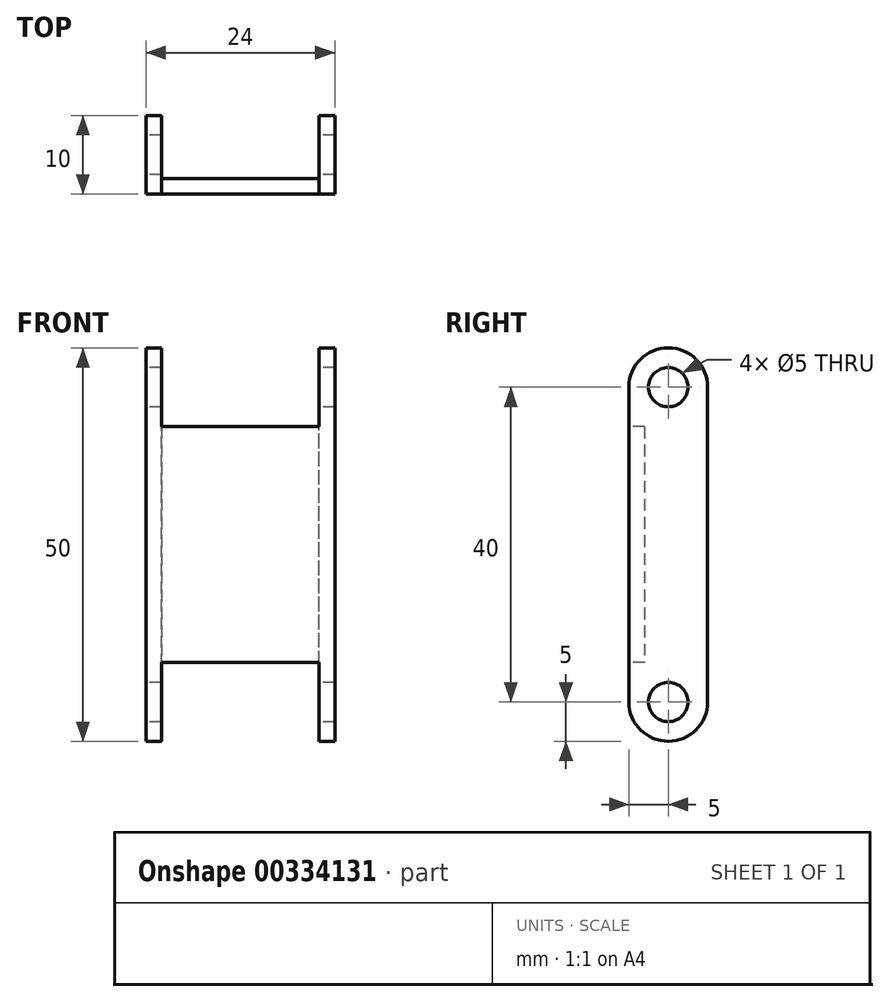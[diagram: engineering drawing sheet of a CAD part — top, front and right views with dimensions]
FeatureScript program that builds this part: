
annotation { "Feature Type Name" : "Feature", "Feature Type Description" : "" }
export const myFeature = defineFeature(function(context is Context, id is Id, definition is map)
    precondition{}
    {
        {
            var Q0;
            Q0=qCreatedBy(makeId("Front.planeOp"),FACE);
            var sketch = newSketch(context, id + "F0", { "sketchPlane" : qUnion([Q0])});
            skLineSegment(sketch, "E0.bottom", {"start": v(0, 0) * mm, "end": v(2, 0) * mm});
            skLineSegment(sketch, "E0.top", {"start": v(0, 50) * mm, "end": v(2, 50) * mm});
            skLineSegment(sketch, "E0.left", {"start": v(0, 0) * mm, "end": v(0, 50) * mm});
            skLineSegment(sketch, "E0.right", {"start": v(2, 0) * mm, "end": v(2, 50) * mm});
            skLineSegment(sketch, "E1.bottom", {"start": v(2, 40) * mm, "end": v(22, 40) * mm});
            skLineSegment(sketch, "E1.top", {"start": v(2, 10) * mm, "end": v(22, 10) * mm});
            skLineSegment(sketch, "E1.left", {"start": v(2, 40) * mm, "end": v(2, 10) * mm});
            skLineSegment(sketch, "E1.right", {"start": v(22, 40) * mm, "end": v(22, 10) * mm});
            skPoint(sketch, "E1.middle", {"position": v(12, 25) * mm});
            skPoint(sketch, "E1.middle.positionSnap0", {"position": v(2, 25) * mm});
            skPoint(sketch, "E1.centerSnap0", {"position": v(2, 25) * mm});
            skLineSegment(sketch, "E2", {"start": v(12, 42.57) * mm, "end": v(12, 7.33) * mm, "construction": true});
            skLineSegment(sketch, "E3.MirrorCS", {"start": v(22, 0) * mm, "end": v(22, 50) * mm});
            skLineSegment(sketch, "E4.MirrorCS", {"start": v(24, 50) * mm, "end": v(22, 50) * mm});
            skLineSegment(sketch, "E5.MirrorCS", {"start": v(24, 0) * mm, "end": v(24, 50) * mm});
            skLineSegment(sketch, "E6.MirrorCS", {"start": v(24, 0) * mm, "end": v(22, 0) * mm});
            skSolve(sketch);
        }
        {
            var Q0;
            {var subQ1=sQuery(id+"F0.wireOp",EDGE,"E0.bottom");Q0=makeQuery(id+"F0.imprint","IMPRINT",FACE,{"disambiguationData":[TD([[makeQuery(id+"F0.imprint","IMPRINT",EDGE,{"derivedFrom":subQ1}),1.0]])]});}
            var Q1;
            {var subQ0=sQuery(id+"F0.wireOp",EDGE,"E4.MirrorCS");Q1=makeQuery(id+"F0.imprint","IMPRINT",FACE,{"disambiguationData":[TD([[makeQuery(id+"F0.imprint","IMPRINT",EDGE,{"derivedFrom":subQ0}),1.0]])]});}
            extrude(context, id + "F1", {"entities" : qUnion([Q0, Q1]), "depth" : 10 * mm, "symmetric" : true});
        }
        {
            var Q0;
            Q0=makeQuery(id+"F1.opExtrude","SWEPT_FACE",FACE,{"disambiguationData":[OSD([sQuery(id+"F0.wireOp",EDGE,"E0.left")])]});
            var sketch = newSketch(context, id + "F2", { "sketchPlane" : qUnion([Q0])});
            skArc(sketch, "E7", {"start": v(-5, 5) * mm, "mid": v(0, 0) * mm, "end": v(5, 5) * mm});
            skLineSegment(sketch, "E8.0", {"start": v(5, 0) * mm, "end": v(5, 5) * mm});
            skLineSegment(sketch, "E9.0", {"start": v(-5, 0) * mm, "end": v(-5, 5) * mm});
            skLineSegment(sketch, "E10.0", {"start": v(5, 0) * mm, "end": v(-5, 0) * mm});
            skPoint(sketch, "E11.orphan", {"position": v(5, 50) * mm});
            skPoint(sketch, "E12.orphan", {"position": v(-5, 50) * mm});
            skSolve(sketch);
        }
        {
            var Q0;
            Q0 = qSketchRegion(id + "F2", true);
            extrude(context, id + "F3", {"entities" : qUnion([Q0]), "operationType" : NewBodyOperationType.REMOVE, "oppositeDirection" : true, "depth" : 25 * mm});
        }
        {
            var Q0;
            Q0=makeQuery(id+"F1.opExtrude","SWEPT_FACE",FACE,{"disambiguationData":[OSD([sQuery(id+"F0.wireOp",EDGE,"E0.left")])]});
            var sketch = newSketch(context, id + "F4", { "sketchPlane" : qUnion([Q0])});
            skArc(sketch, "E13", {"start": v(5, 45) * mm, "mid": v(0, 50) * mm, "end": v(-5, 45) * mm});
            skLineSegment(sketch, "E14.0", {"start": v(5, 50) * mm, "end": v(-5, 50) * mm});
            skLineSegment(sketch, "E15.0", {"start": v(-5, 45) * mm, "end": v(-5, 50) * mm});
            skLineSegment(sketch, "E16.0", {"start": v(5, 45) * mm, "end": v(5, 50) * mm});
            skPoint(sketch, "E17.orphan", {"position": v(5, 5) * mm});
            skPoint(sketch, "E18.orphan", {"position": v(-5, 5) * mm});
            skSolve(sketch);
        }
        {
            var Q0;
            Q0 = qSketchRegion(id + "F4", true);
            extrude(context, id + "F5", {"entities" : qUnion([Q0]), "operationType" : NewBodyOperationType.REMOVE, "oppositeDirection" : true, "depth" : 25 * mm});
        }
        {
            var Q0;
            Q0=makeQuery(id+"F1.opExtrude","SWEPT_FACE",FACE,{"disambiguationData":[OSD([sQuery(id+"F0.wireOp",EDGE,"E0.left")])]});
            var sketch = newSketch(context, id + "F6", { "sketchPlane" : qUnion([Q0])});
            skCircle(sketch, "E19", {"center": v(0, 45) * mm, "radius": 2.5 * mm});
            skSolve(sketch);
        }
        {
            var Q0;
            Q0 = qSketchRegion(id + "F6", true);
            extrude(context, id + "F7", {"entities" : qUnion([Q0]), "operationType" : NewBodyOperationType.REMOVE, "oppositeDirection" : true, "depth" : 25 * mm});
        }
        {
            var Q0;
            Q0=makeQuery(id+"F1.opExtrude","SWEPT_FACE",FACE,{"disambiguationData":[OSD([sQuery(id+"F0.wireOp",EDGE,"E0.left")])]});
            var sketch = newSketch(context, id + "F8", { "sketchPlane" : qUnion([Q0])});
            skCircle(sketch, "E20", {"center": v(0, 5) * mm, "radius": 2.5 * mm});
            skSolve(sketch);
        }
        {
            var Q0;
            Q0 = qSketchRegion(id + "F8", true);
            extrude(context, id + "F9", {"entities" : qUnion([Q0]), "operationType" : NewBodyOperationType.REMOVE, "oppositeDirection" : true, "depth" : 25 * mm});
        }
        {
            var Q0;
            Q0=makeQuery(id+"F1.opExtrude","CAP_FACE",FACE,{"disambiguationData":[OSD([sQuery(id+"F0.wireOp",EDGE,"E3.MirrorCS"),sQuery(id+"F0.wireOp",EDGE,"E4.MirrorCS"),sQuery(id+"F0.wireOp",EDGE,"E5.MirrorCS"),sQuery(id+"F0.wireOp",EDGE,"E6.MirrorCS")])],"isStart":false});
            var sketch = newSketch(context, id + "F10", { "sketchPlane" : qUnion([Q0])});
            skLineSegment(sketch, "E21.0", {"start": v(2, 40) * mm, "end": v(22, 40) * mm});
            skLineSegment(sketch, "E22.0", {"start": v(2, 10) * mm, "end": v(22, 10) * mm});
            skLineSegment(sketch, "E23.0", {"start": v(2, 40) * mm, "end": v(2, 10) * mm});
            skLineSegment(sketch, "E24.0", {"start": v(22, 10) * mm, "end": v(22, 40) * mm});
            skPoint(sketch, "E25.orphan", {"position": v(22, 50) * mm});
            skPoint(sketch, "E26.orphan", {"position": v(22, 0) * mm});
            skSolve(sketch);
        }
        {
            var Q0;
            Q0 = qSketchRegion(id + "F10", true);
            extrude(context, id + "F11", {"entities" : qUnion([Q0]), "oppositeDirection" : true, "depth" : 2 * mm});
        }
        {
            var Q0;
            Q0=makeQuery(id+"F1.opExtrude","SWEPT_BODY",BODY,{"disambiguationData":[OSD([sQuery(id+"F0.wireOp",EDGE,"E0.bottom"),sQuery(id+"F0.wireOp",EDGE,"E0.top"),sQuery(id+"F0.wireOp",EDGE,"E0.left"),sQuery(id+"F0.wireOp",EDGE,"E0.right"),sQuery(id+"F0.wireOp",EDGE,"E1.left")])]});
            var Q1;
            Q1=makeQuery(id+"F1.opExtrude","SWEPT_BODY",BODY,{"disambiguationData":[OSD([sQuery(id+"F0.wireOp",EDGE,"E3.MirrorCS"),sQuery(id+"F0.wireOp",EDGE,"E4.MirrorCS"),sQuery(id+"F0.wireOp",EDGE,"E5.MirrorCS"),sQuery(id+"F0.wireOp",EDGE,"E6.MirrorCS")])]});
            var Q2;
            Q2=makeQuery(id+"F11.opExtrude","SWEPT_BODY",BODY,{"disambiguationData":[OSD([sQuery(id+"F10.wireOp",EDGE,"E21.0"),sQuery(id+"F10.wireOp",EDGE,"E22.0"),sQuery(id+"F10.wireOp",EDGE,"E23.0"),sQuery(id+"F10.wireOp",EDGE,"E24.0")])]});
            booleanBodies(context, id + "F12", {"operationType" : BooleanOperationType.UNION, "tools" : qUnion([Q0, Q1, Q2])});
        }
        {
            var Q0;
            Q0=makeQuery(id+"F1.opExtrude","SWEPT_FACE",FACE,{"disambiguationData":[OSD([sQuery(id+"F0.wireOp",EDGE,"E5.MirrorCS")])]});
            var sketch = newSketch(context, id + "F13", { "sketchPlane" : qUnion([Q0])});
            skArc(sketch, "E27", {"start": v(5, 45) * mm, "mid": v(0, 50) * mm, "end": v(-5, 45) * mm});
            skCircle(sketch, "E28", {"center": v(0, 45) * mm, "radius": 2.5 * mm});
            skArc(sketch, "E29", {"start": v(-5, 5) * mm, "mid": v(0, 0) * mm, "end": v(5, 5) * mm});
            skCircle(sketch, "E30", {"center": v(0, 5) * mm, "radius": 2.5 * mm});
            skLineSegment(sketch, "E31.0", {"start": v(-5, 50) * mm, "end": v(5, 50) * mm});
            skLineSegment(sketch, "E32.0", {"start": v(5, 0) * mm, "end": v(5, 5) * mm});
            skLineSegment(sketch, "E33.0", {"start": v(-5, 0) * mm, "end": v(-5, 5) * mm});
            skLineSegment(sketch, "E34.0", {"start": v(-5, 0) * mm, "end": v(5, 0) * mm});
            skLineSegment(sketch, "E35.trimOffspring", {"start": v(-5, 45) * mm, "end": v(-5, 50) * mm});
            skLineSegment(sketch, "E36.trimOffspring", {"start": v(5, 45) * mm, "end": v(5, 50) * mm});
            skSolve(sketch);
        }
        {
            var Q0;
            Q0 = qSketchRegion(id + "F13", true);
            extrude(context, id + "F14", {"entities" : qUnion([Q0]), "operationType" : NewBodyOperationType.REMOVE, "oppositeDirection" : true, "depth" : 10 * mm});
        }
    });
